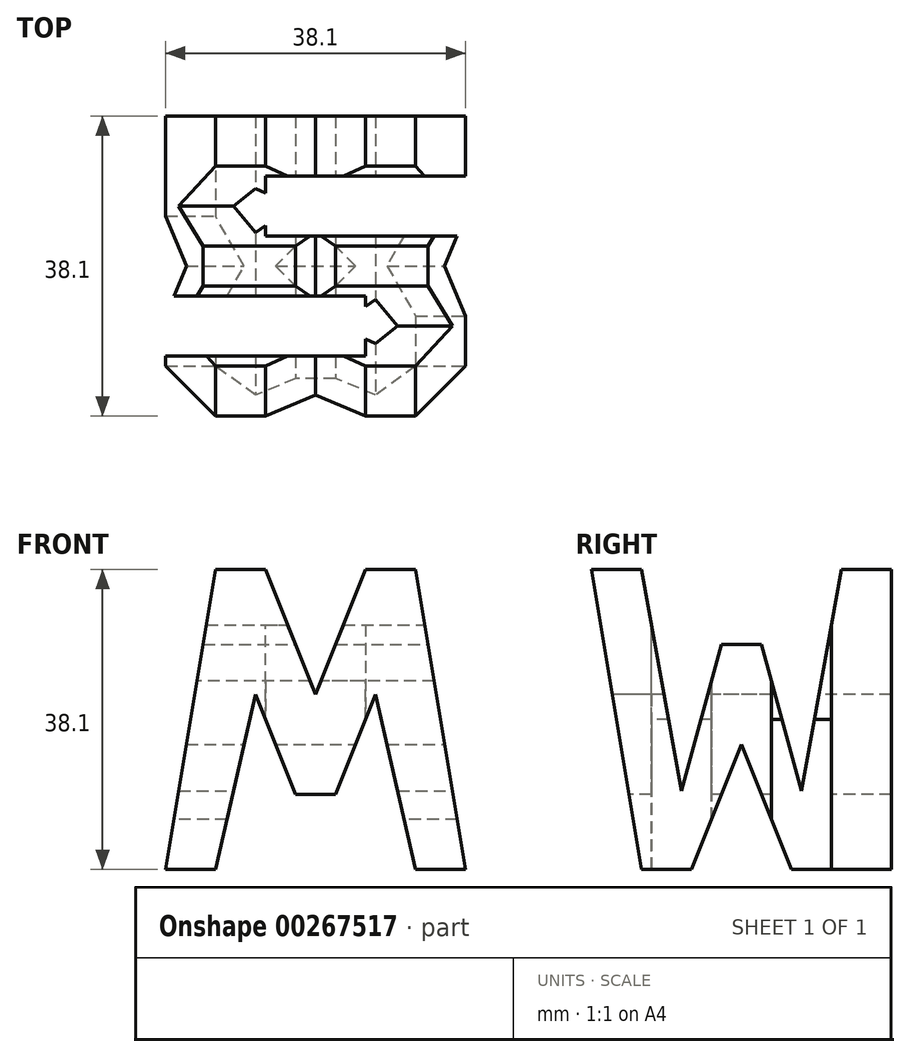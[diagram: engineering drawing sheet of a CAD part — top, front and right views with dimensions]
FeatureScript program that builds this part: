
annotation { "Feature Type Name" : "Feature", "Feature Type Description" : "" }
export const myFeature = defineFeature(function(context is Context, id is Id, definition is map)
    precondition{}
    {
        {
            var Q0;
            Q0=qCreatedBy(makeId("Front.planeOp"),FACE);
            var sketch = newSketch(context, id + "F0", { "sketchPlane" : qUnion([Q0])});
            skLineSegment(sketch, "E0", {"start": v(0, 0) * mm, "end": v(0, -38.1) * mm});
            skLineSegment(sketch, "E1", {"start": v(0, -38.1) * mm, "end": v(38.1, -38.1) * mm});
            skLineSegment(sketch, "E2", {"start": v(38.1, -38.1) * mm, "end": v(38.1, 0) * mm});
            skLineSegment(sketch, "E3", {"start": v(38.1, 0) * mm, "end": v(0, 0) * mm});
            skSolve(sketch);
        }
        {
            var Q0;
            Q0 = qSketchRegion(id + "F0", true);
            extrude(context, id + "F1", {"entities" : qUnion([Q0]), "depth" : 38.1 * mm});
        }
        {
            var Q0;
            Q0=qCreatedBy(makeId("Front.planeOp"),FACE);
            cPlane(context, id + "F2", {"entities" : qUnion([Q0]), "cplaneType" : CPlaneType.OFFSET, "offset" : 38.1 * mm, "width" : 152.4 * mm, "height" : 152.4 * mm});
        }
        {
            var Q0;
            Q0=qCreatedBy(makeId("Right.planeOp"),FACE);
            cPlane(context, id + "F3", {"entities" : qUnion([Q0]), "cplaneType" : CPlaneType.OFFSET, "offset" : 38.1 * mm, "width" : 152.4 * mm, "height" : 152.4 * mm});
        }
        {
            var Q0;
            Q0=qCreatedBy(id+"F3.planeOp",FACE);
            var sketch = newSketch(context, id + "F4", { "sketchPlane" : qUnion([Q0])});
            skLineSegment(sketch, "E4", {"start": v(0, 0) * mm, "end": v(0, -32.93) * mm});
            skLineSegment(sketch, "E5", {"start": v(-38.1, 0) * mm, "end": v(0, 0) * mm});
            skLineSegment(sketch, "E6", {"start": v(-38.1, 0) * mm, "end": v(-31.75, -38.1) * mm});
            skLineSegment(sketch, "E7", {"start": v(-31.75, 0) * mm, "end": v(-26.67, -28.1) * mm});
            skLineSegment(sketch, "E8", {"start": v(-26.67, -28.1) * mm, "end": v(-21.6, -9.52) * mm});
            skLineSegment(sketch, "E9", {"start": v(-21.6, -9.52) * mm, "end": v(-16.51, -9.52) * mm});
            skLineSegment(sketch, "E10", {"start": v(-16.51, -9.52) * mm, "end": v(-11.43, -28.1) * mm});
            skLineSegment(sketch, "E11", {"start": v(-11.43, -28.1) * mm, "end": v(-6.35, 0) * mm});
            skLineSegment(sketch, "E12", {"start": v(0, 0) * mm, "end": v(-6.35, -38.1) * mm});
            skLineSegment(sketch, "E13", {"start": v(-25.4, -38.1) * mm, "end": v(-19.05, -22.22) * mm});
            skLineSegment(sketch, "E14", {"start": v(-19.05, -22.22) * mm, "end": v(-12.7, -38.1) * mm});
            skLineSegment(sketch, "E15", {"start": v(-38.1, 0) * mm, "end": v(-38.1, -38.1) * mm});
            skLineSegment(sketch, "E16", {"start": v(-38.1, -38.1) * mm, "end": v(0, -38.1) * mm});
            skLineSegment(sketch, "E17", {"start": v(0, -38.1) * mm, "end": v(0, 0) * mm});
            skLineSegment(sketch, "E18", {"start": v(-6.35, -38.1) * mm, "end": v(0, 0) * mm});
            skSolve(sketch);
        }
        {
            var Q0;
            {var subQ0=sQuery(id+"F4.wireOp",EDGE,"E6");Q0=makeQuery(id+"F4.imprint","IMPRINT",FACE,{"disambiguationData":[TD([[makeQuery(id+"F4.imprint","IMPRINT",EDGE,{"derivedFrom":subQ0}),-1.0]])]});}
            var Q1;
            {var subQ0=sQuery(id+"F4.wireOp",EDGE,"E7");Q1=makeQuery(id+"F4.imprint","IMPRINT",FACE,{"disambiguationData":[TD([[makeQuery(id+"F4.imprint","IMPRINT",EDGE,{"derivedFrom":subQ0}),1.0]])]});}
            var Q2;
            {var subQ0=sQuery(id+"F4.wireOp",EDGE,"E13");Q2=makeQuery(id+"F4.imprint","IMPRINT",FACE,{"disambiguationData":[TD([[makeQuery(id+"F4.imprint","IMPRINT",EDGE,{"derivedFrom":subQ0}),-1.0]])]});}
            var Q3;
            {var subQ3=sQuery(id+"F4.wireOp",EDGE,"E18");Q3=makeQuery(id+"F4.imprint","IMPRINT",FACE,{"disambiguationData":[TD([[makeQuery(id+"F4.imprint","IMPRINT",EDGE,{"derivedFrom":subQ3}),-1.0]])]});}
            extrude(context, id + "F5", {"entities" : qUnion([Q0, Q1, Q2, Q3]), "operationType" : NewBodyOperationType.REMOVE, "oppositeDirection" : true, "depth" : 38.1 * mm});
        }
        {
            var Q0;
            Q0=qCreatedBy(id+"F2.planeOp",FACE);
            var sketch = newSketch(context, id + "F6", { "sketchPlane" : qUnion([Q0])});
            skLineSegment(sketch, "E19", {"start": v(0, 0) * mm, "end": v(38.1, 0) * mm});
            skLineSegment(sketch, "E20", {"start": v(38.1, 0) * mm, "end": v(38.1, -38.1) * mm});
            skLineSegment(sketch, "E21", {"start": v(38.1, -38.1) * mm, "end": v(0, -38.1) * mm});
            skLineSegment(sketch, "E22", {"start": v(0, -38.1) * mm, "end": v(0, 0) * mm});
            skLineSegment(sketch, "E23", {"start": v(0, -38.1) * mm, "end": v(6.35, 0) * mm});
            skLineSegment(sketch, "E24", {"start": v(12.7, 0) * mm, "end": v(19.05, -15.87) * mm});
            skLineSegment(sketch, "E25", {"start": v(19.05, -15.87) * mm, "end": v(25.4, 0) * mm});
            skLineSegment(sketch, "E26", {"start": v(31.75, 0) * mm, "end": v(38.1, -38.1) * mm});
            skLineSegment(sketch, "E27", {"start": v(31.75, -38.1) * mm, "end": v(26.67, -15.88) * mm});
            skLineSegment(sketch, "E28", {"start": v(26.67, -15.88) * mm, "end": v(21.59, -28.58) * mm});
            skLineSegment(sketch, "E29", {"start": v(21.6, -28.57) * mm, "end": v(16.51, -28.57) * mm});
            skLineSegment(sketch, "E30", {"start": v(16.51, -28.58) * mm, "end": v(11.43, -15.88) * mm});
            skLineSegment(sketch, "E31", {"start": v(11.43, -15.88) * mm, "end": v(6.35, -38.1) * mm});
            skSolve(sketch);
        }
        {
            var Q0;
            {var subQ0=sQuery(id+"F6.wireOp",EDGE,"E22");Q0=makeQuery(id+"F6.imprint","IMPRINT",FACE,{"disambiguationData":[TD([[makeQuery(id+"F6.imprint","IMPRINT",EDGE,{"derivedFrom":subQ0}),-1.0]])]});}
            var Q1;
            {var subQ0=sQuery(id+"F6.wireOp",EDGE,"E24");Q1=makeQuery(id+"F6.imprint","IMPRINT",FACE,{"disambiguationData":[TD([[makeQuery(id+"F6.imprint","IMPRINT",EDGE,{"derivedFrom":subQ0}),1.0]])]});}
            var Q2;
            {var subQ0=sQuery(id+"F6.wireOp",EDGE,"E27");Q2=makeQuery(id+"F6.imprint","IMPRINT",FACE,{"disambiguationData":[TD([[makeQuery(id+"F6.imprint","IMPRINT",EDGE,{"derivedFrom":subQ0}),1.0]])]});}
            var Q3;
            {var subQ0=sQuery(id+"F6.wireOp",EDGE,"E20");Q3=makeQuery(id+"F6.imprint","IMPRINT",FACE,{"disambiguationData":[TD([[makeQuery(id+"F6.imprint","IMPRINT",EDGE,{"derivedFrom":subQ0}),-1.0]])]});}
            extrude(context, id + "F7", {"entities" : qUnion([Q0, Q1, Q2, Q3]), "operationType" : NewBodyOperationType.REMOVE, "oppositeDirection" : true, "depth" : 38.1 * mm});
        }
        {
            var Q0;
            Q0=qCreatedBy(makeId("Top.planeOp"),FACE);
            var sketch = newSketch(context, id + "F8", { "sketchPlane" : qUnion([Q0])});
            skLineSegment(sketch, "E32", {"start": v(0, 0) * mm, "end": v(38.1, 0) * mm});
            skLineSegment(sketch, "E33", {"start": v(38.1, 0) * mm, "end": v(38.1, -38.1) * mm});
            skLineSegment(sketch, "E34", {"start": v(38.1, -38.1) * mm, "end": v(0, -38.1) * mm});
            skLineSegment(sketch, "E35", {"start": v(0, -38.1) * mm, "end": v(0, 0) * mm});
            skLineSegment(sketch, "E36", {"start": v(38.1, -7.62) * mm, "end": v(12.7, -7.62) * mm});
            skLineSegment(sketch, "E37", {"start": v(12.7, -7.62) * mm, "end": v(12.7, -15.24) * mm});
            skLineSegment(sketch, "E38", {"start": v(12.7, -15.24) * mm, "end": v(38.1, -15.24) * mm});
            skLineSegment(sketch, "E39", {"start": v(0, -22.86) * mm, "end": v(25.4, -22.86) * mm});
            skLineSegment(sketch, "E40", {"start": v(25.4, -22.86) * mm, "end": v(25.4, -30.48) * mm});
            skLineSegment(sketch, "E41", {"start": v(25.4, -30.48) * mm, "end": v(0, -30.48) * mm});
            skSolve(sketch);
        }
        {
            var Q0;
            {var subQ0=sQuery(id+"F8.wireOp",EDGE,"E36");Q0=makeQuery(id+"F8.imprint","IMPRINT",FACE,{"disambiguationData":[TD([[makeQuery(id+"F8.imprint","IMPRINT",EDGE,{"derivedFrom":subQ0}),1.0]])]});}
            var Q1;
            {var subQ0=sQuery(id+"F8.wireOp",EDGE,"E39");Q1=makeQuery(id+"F8.imprint","IMPRINT",FACE,{"disambiguationData":[TD([[makeQuery(id+"F8.imprint","IMPRINT",EDGE,{"derivedFrom":subQ0}),-1.0]])]});}
            extrude(context, id + "F9", {"entities" : qUnion([Q0, Q1]), "operationType" : NewBodyOperationType.REMOVE, "oppositeDirection" : true, "depth" : 38.1 * mm});
        }
    });
